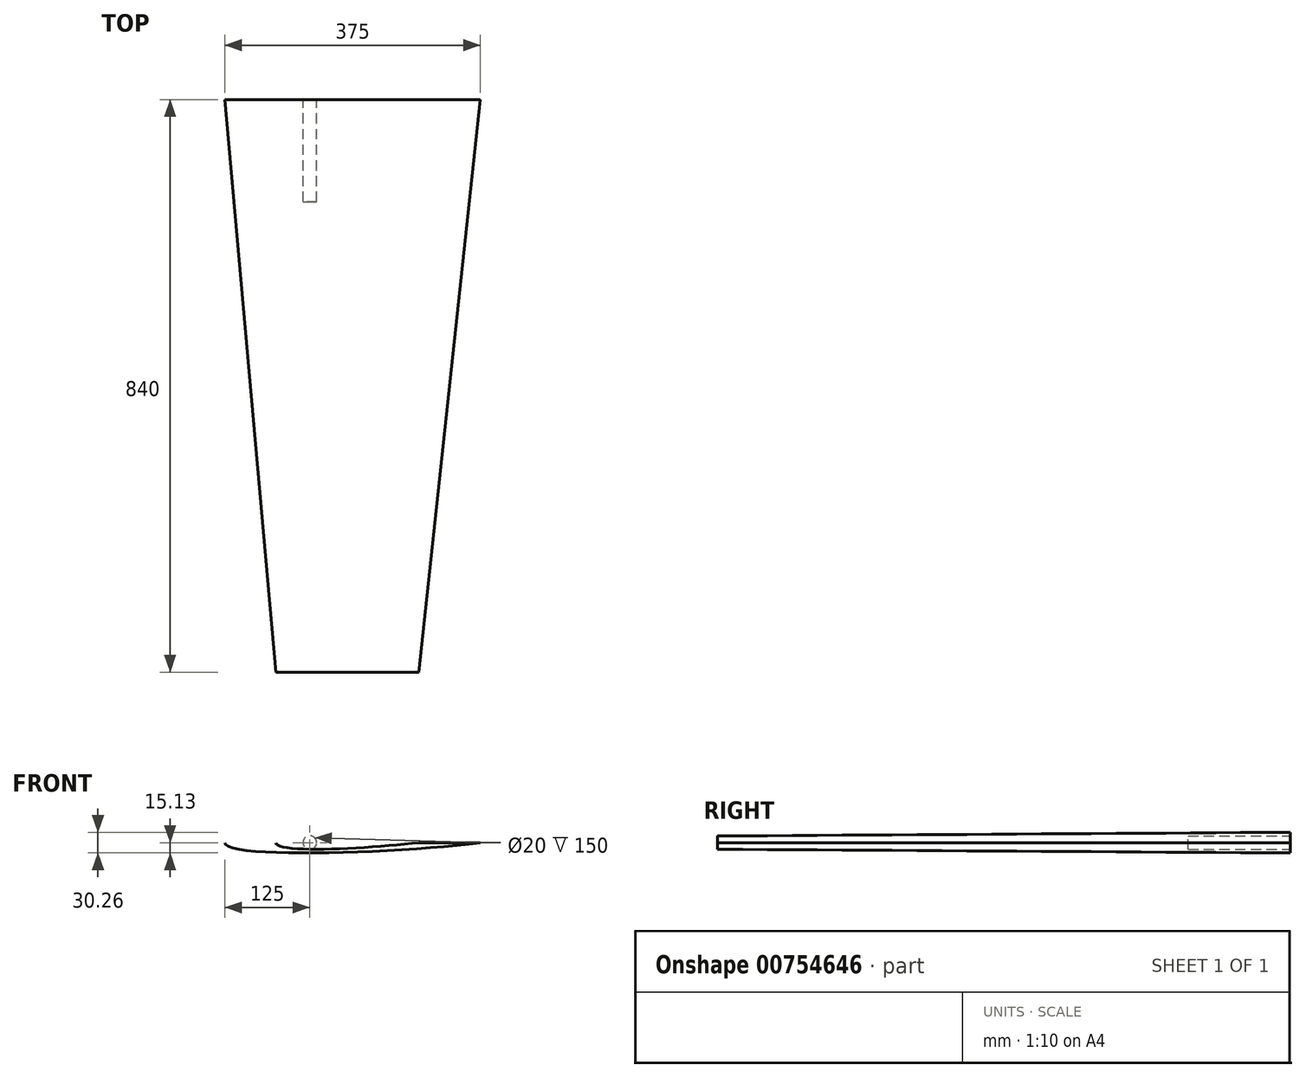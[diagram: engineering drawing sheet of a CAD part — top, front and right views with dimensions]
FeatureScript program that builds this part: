
annotation { "Feature Type Name" : "Feature", "Feature Type Description" : "" }
export const myFeature = defineFeature(function(context is Context, id is Id, definition is map)
    precondition{}
    {
        {
            var Q0;
            Q0=qCreatedBy(makeId("Front.planeOp"),FACE);
            var sketch = newSketch(context, id + "F0", { "sketchPlane" : qUnion([Q0])});
            skCircle(sketch, "E0", {"center": v(0, 0) * mm, "radius": 10 * mm, "construction": true});
            skLineSegment(sketch, "E1", {"start": v(-169.18, 0) * mm, "end": v(221.14, 0) * mm, "construction": true});
            skLineSegment(sketch, "E2", {"start": v(-125, -56.36) * mm, "end": v(-125, 55.1) * mm, "construction": true});
            skLineSegment(sketch, "E3", {"start": v(250, -27.97) * mm, "end": v(250, 27.97) * mm, "construction": true});
            skPoint(sketch, "E4.0.internal.snap0", {"position": v(-125, -0.63) * mm});
            skFitSpline(sketch, "E4", {"points": [v(-125, 0) * mm, v(250, 0) * mm], "startDerivative": vector(0, 72.47) * mm, "endDerivative": vector(361.41, -47.3) * mm});
            skFitSpline(sketch, "E5.MirrorCS", {"points": [v(-125, 0) * mm, v(250, 0) * mm], "startDerivative": vector(0, -72.47) * mm, "endDerivative": vector(361.41, 47.3) * mm});
            skSolve(sketch);
        }
        {
            var Q0;
            Q0=qCreatedBy(makeId("Front.planeOp"),FACE);
            cPlane(context, id + "F1", {"entities" : qUnion([Q0]), "cplaneType" : CPlaneType.OFFSET, "offset" : 840 * mm, "width" : 150 * mm, "height" : 150 * mm});
        }
        {
            var Q0;
            Q0=qCreatedBy(id+"F1.planeOp",FACE);
            var sketch = newSketch(context, id + "F2", { "sketchPlane" : qUnion([Q0])});
            skLineSegment(sketch, "E6.0", {"start": v(-169.18, 0) * mm, "end": v(221.14, 0) * mm, "construction": true});
            skPoint(sketch, "E7.0", {"position": v(0, 0) * mm});
            skLineSegment(sketch, "E8", {"start": v(-50, -30.4) * mm, "end": v(-50, 38.14) * mm, "construction": true});
            skLineSegment(sketch, "E9", {"start": v(160, -36.41) * mm, "end": v(160, 50.56) * mm, "construction": true});
            skFitSpline(sketch, "E10", {"points": [v(-50, 0) * mm, v(160, 0) * mm], "startDerivative": vector(0, 49.17) * mm, "endDerivative": vector(229.98, -26.53) * mm});
            skFitSpline(sketch, "E11.MirrorCS", {"points": [v(-50, 0) * mm, v(160, 0) * mm], "startDerivative": vector(0, -49.17) * mm, "endDerivative": vector(229.98, 26.53) * mm});
            skSolve(sketch);
        }
        {
            var Q0;
            Q0 = qSketchRegion(id + "F0", true);
            var Q1;
            Q1 = qSketchRegion(id + "F2", true);
            loft(context, id + "F3", {"sheetProfilesArray" : [{ "sheetProfileEntities" : qUnion([Q0]) }, { "sheetProfileEntities" : qUnion([Q1]) }]});
        }
        {
            var Q0;
            Q0=makeQuery(id+"F0.imprint","IMPRINT",FACE,{"disambiguationData":[TD([[makeQuery(id+"F0.imprint","IMPRINT",EDGE,{"derivedFrom":sQuery(id+"F0.wireOp",EDGE,"E4")}),-1.0]])]});
            var sketch = newSketch(context, id + "F4", { "sketchPlane" : qUnion([Q0])});
            skCircle(sketch, "E12.0", {"center": v(0, 0) * mm, "radius": 10 * mm});
            skSolve(sketch);
        }
        {
            var Q0;
            Q0 = qSketchRegion(id + "F4", true);
            extrude(context, id + "F5", {"entities" : qUnion([Q0]), "operationType" : NewBodyOperationType.REMOVE, "depth" : 150 * mm, "offsetDistance" : 25 * mm});
        }
    });
